# Revit family: DCS_Revit_18_GDE1-30-N_or_L_Grill_90000774A
name_source: partatom
category: Specialty Equipment
revit_build: Autodesk Revit 2018 (Build: 20170223_1515(x64)
units: mm (PartAtom-declared; Revit-internal decimal feet)

## family parameters
Always vertical = Yes
Cut with Voids When Loaded = Yes
OmniClass Number = 23.40.40.14.17.27
OmniClass Title = Barbecues
Part Type = Normal
Room Calculation Point = No
Round Connector Dimension = Use Diameter
Shared = No
Work Plane-Based = No

## types (4) — shared parameters
Clearance - Below Combustible = 305 mm  [stored 1.00066 ft]
Clearance - Rear Combustible = 305 mm  [stored 1.00066 ft]
Clearance - Rear Non-Combustible = 76 mm  [stored 0.249344 ft]
Clearance - Side Combustible = 305 mm  [stored 1.00066 ft]
Clearance - Side Non-Combustible = 152 mm  [stored 0.498688 ft]
Connector Description - Electrical = 120 V, 15 A, GFI electrical outlet
Connector Description - Gas = Operating Pressure NG 4” WC, LPG 11” WC, Connection is 1/2” NPT female
Manufacturer = Fisher & Paykel
Material - Body = DCS - Stainless Steel
URL = www.dcsappliances.com
Visibility - Clearance Required = Yes

## per-type parameters (varying)
| type | Cavity - Depth | Cavity - Height | Cavity - Width | Description | Model | Product - Depth | Product - Height | Product - Width | Visibility - Clearance Required (Below Countertop) | Visibility - Cover | Visibility - Insulation Jacket |
| Griddle (without covers) | 578 mm  [stored 1.89633 ft] | 257 mm  [stored 0.843176 ft] | 724 mm  [stored 2.37533 ft] | 30" Griddle | GDE1-30-N or GDE1-30-L | 692 mm | 312 mm | 762 mm  [stored 2.5 ft] | Yes | No | No |
| Griddle with Insulated Jacket (without covers) | 603 mm | 283 mm | 886 mm  [stored 2.90682 ft] | 30" Griddle with 30" Inslated Jacket | GDE1-30-N or GDE1-30-L with BGB30IJS | 699 mm | 342 mm | 880 mm  [stored 2.88714 ft] | No | No | Yes |
| Griddle with Insulated Jacket | 603 mm | 283 mm | 886 mm  [stored 2.90682 ft] | 30" Griddle with 30" Inslated Jacket | GDE1-30-N or GDE1-30-L with BGB30IJS | 699 mm | 342 mm | 880 mm  [stored 2.88714 ft] | No | Yes | Yes |
| Griddle | 578 mm  [stored 1.89633 ft] | 257 mm  [stored 0.843176 ft] | 724 mm  [stored 2.37533 ft] | 30" Griddle | GDE1-30-N or GDE1-30-L | 692 mm | 312 mm | 762 mm  [stored 2.5 ft] | Yes | Yes | No |

note: [stored X ft] marks values corroborated as IEEE doubles in the binary element streams (Revit-internal decimal feet)

## geometry (parser evidence)
native form markers: Blend x2, Sweep x18
no freeform markers — native parametric forms only
